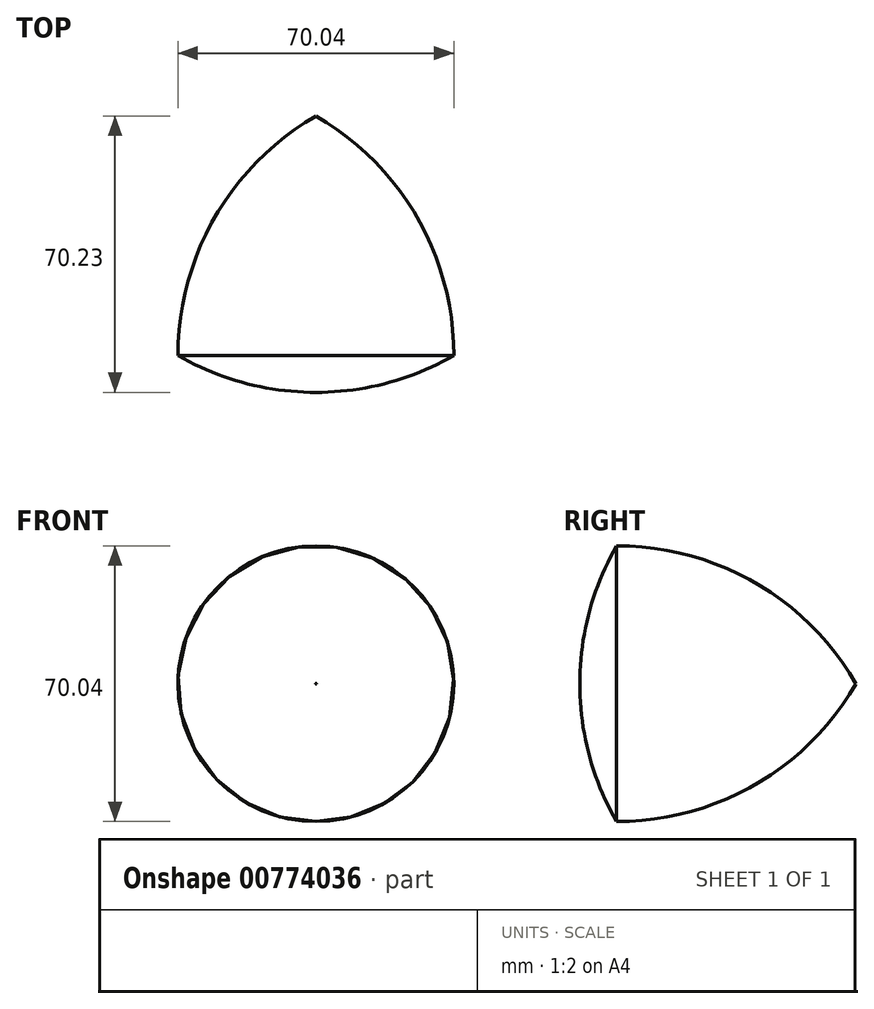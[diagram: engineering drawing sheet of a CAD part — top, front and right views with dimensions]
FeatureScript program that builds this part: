
annotation { "Feature Type Name" : "Feature", "Feature Type Description" : "" }
export const myFeature = defineFeature(function(context is Context, id is Id, definition is map)
    precondition{}
    {
        {
            var Q0;
            Q0=qCreatedBy(makeId("Top.planeOp"),FACE);
            var sketch = newSketch(context, id + "F0", { "sketchPlane" : qUnion([Q0])});
            skLineSegment(sketch, "E0", {"start": v(0, 60.62) * mm, "end": v(-35, 0) * mm});
            skLineSegment(sketch, "E1", {"start": v(35, 0) * mm, "end": v(0, 60.62) * mm});
            skLineSegment(sketch, "E2", {"start": v(-35, 0) * mm, "end": v(35, 0) * mm});
            skArc(sketch, "E3", {"start": v(-35.02, -0.19) * mm, "mid": v(0.03, -9.55) * mm, "end": v(35.07, -0.15) * mm});
            skArc(sketch, "E4", {"start": v(0.05, 60.68) * mm, "mid": v(-25.67, 34.96) * mm, "end": v(-35.02, -0.19) * mm});
            skArc(sketch, "E5", {"start": v(35.07, -0.15) * mm, "mid": v(25.73, 34.96) * mm, "end": v(0.05, 60.68) * mm});
            skLineSegment(sketch, "E6", {"start": v(0.05, 60.68) * mm, "end": v(0.05, -9.55) * mm});
            skSolve(sketch);
        }
        {
            var Q0;
            {var subQ0=sQuery(id+"F0.wireOp",EDGE,"E5");Q0=makeQuery(id+"F0.imprint","IMPRINT",FACE,{"disambiguationData":[TD([[makeQuery(id+"F0.imprint","IMPRINT",EDGE,{"derivedFrom":subQ0}),1.0]])]});}
            var Q1;
            {var subQ0=sQuery(id+"F0.wireOp",EDGE,"E2");var subQ1=sQuery(id+"F0.wireOp",EDGE,"E1");var subQ2=makeQuery(id+"F0.imprint","INTERSECT",VERTEX,{"derivedFrom":[subQ1,subQ0]});Q1=makeQuery(id+"F0.imprint","IMPRINT",FACE,{"disambiguationData":[TD([[makeQuery(id+"F0.imprint","IMPRINT",EDGE,{"disambiguationData":[TD([[subQ2,-1.0]])],"derivedFrom":subQ1}),1.0]])]});}
            var Q2;
            Q2=sQuery(id+"F0.wireOp",EDGE,"E6");
            revolve(context, id + "F1", {"surfaceOperationType" : NewSurfaceOperationType.NEW, "entities" : qUnion([Q0, Q1]), "axis" : qUnion([Q2]), "revolveType" : RevolveType.FULL});
        }
    });
